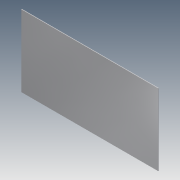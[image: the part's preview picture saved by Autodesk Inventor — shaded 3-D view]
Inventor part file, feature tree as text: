
AUTODESK INVENTOR PART (.ipt)
format: ipt  version: 2014 (Build 180170000, 170)  size: 71,680 bytes
history: native  units: in
note: dims shown in document units (in); Inventor stores cm internally (conversion verified against a paired STEP export)
features: extrude x1, sketch x1
ambient origin geometry x8: Origin, YZ Plane, XZ Plane, XY Plane, X Axis, Y Axis, Z Axis, Center Point
bodies: Solid1 (feature_tree)
feature tree (2):
  extrude  "Extrusion1"  Depth=14.4in
  sketch  "Sketch1"  dims[d0=27.5in d1=14.4in d2=0.125in d3=0.0in]
